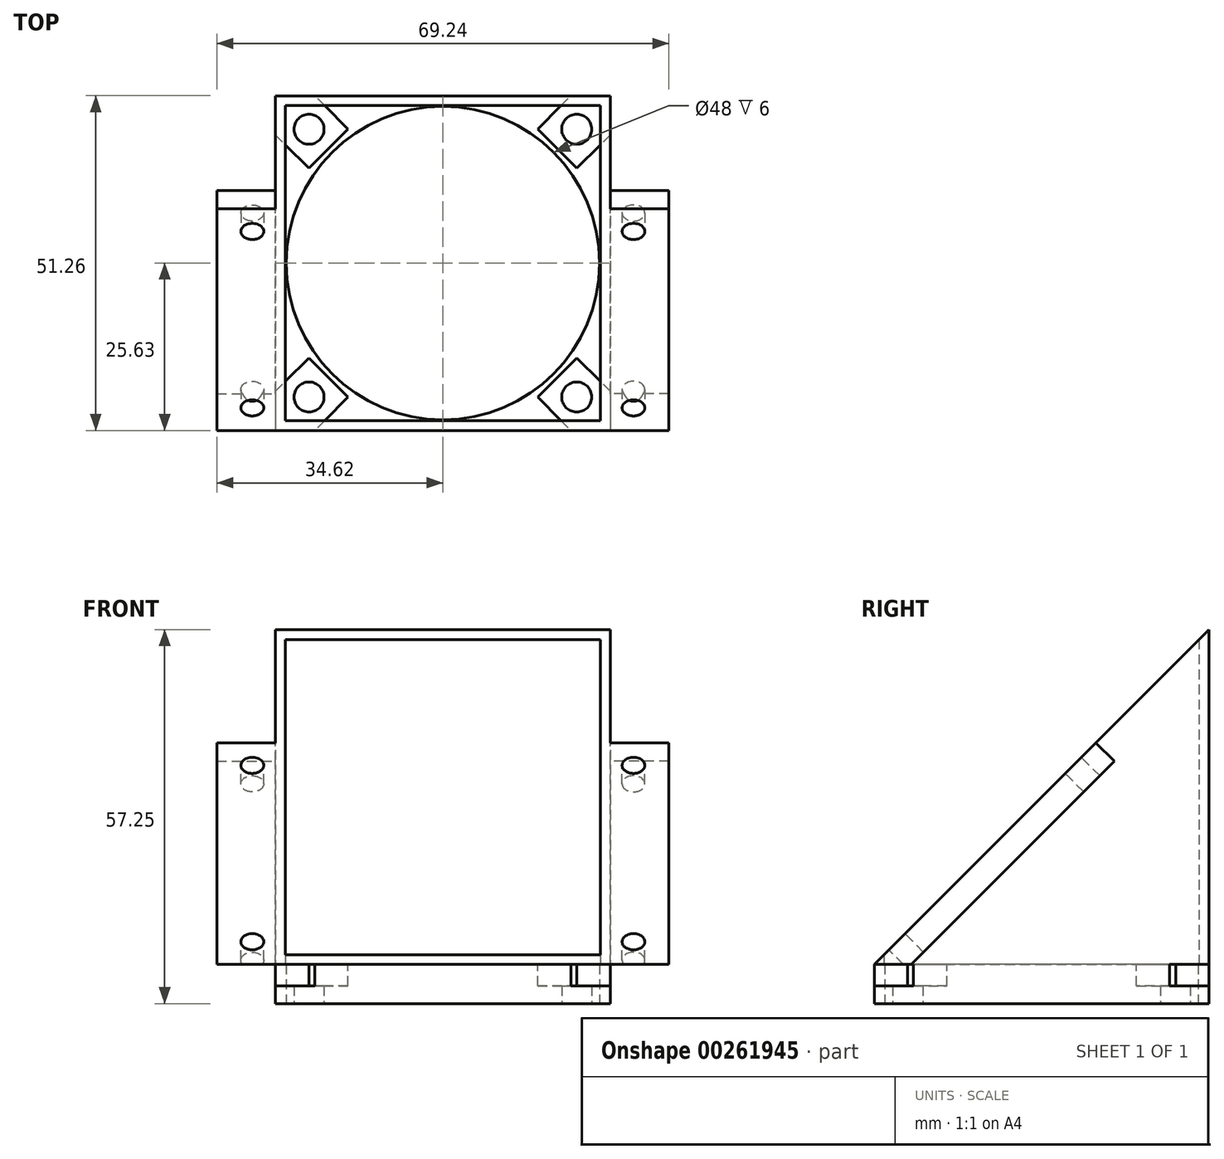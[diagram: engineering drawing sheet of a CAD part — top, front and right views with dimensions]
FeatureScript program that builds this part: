
annotation { "Feature Type Name" : "Feature", "Feature Type Description" : "" }
export const myFeature = defineFeature(function(context is Context, id is Id, definition is map)
    precondition{}
    {
        {
            var Q0;
            Q0=qCreatedBy(makeId("Top.planeOp"),FACE);
            var sketch = newSketch(context, id + "F0", { "sketchPlane" : qUnion([Q0])});
            skLineSegment(sketch, "E0.bottom", {"start": v(-25.63, 25.63) * mm, "end": v(25.63, 25.63) * mm});
            skLineSegment(sketch, "E0.top", {"start": v(-25.63, -25.63) * mm, "end": v(25.63, -25.63) * mm});
            skLineSegment(sketch, "E0.left", {"start": v(-25.63, 25.63) * mm, "end": v(-25.63, -25.63) * mm});
            skLineSegment(sketch, "E0.right", {"start": v(25.63, 25.63) * mm, "end": v(25.63, -25.63) * mm});
            skCircle(sketch, "E1", {"center": v(0, 0) * mm, "radius": 24 * mm});
            skLineSegment(sketch, "E2.bottom", {"start": v(-20.5, 20.5) * mm, "end": v(20.5, 20.5) * mm, "construction": true});
            skLineSegment(sketch, "E2.top", {"start": v(-20.5, -20.5) * mm, "end": v(20.5, -20.5) * mm, "construction": true});
            skLineSegment(sketch, "E2.left", {"start": v(-20.5, 20.5) * mm, "end": v(-20.5, -20.5) * mm, "construction": true});
            skLineSegment(sketch, "E2.right", {"start": v(20.5, 20.5) * mm, "end": v(20.5, -20.5) * mm, "construction": true});
            skCircle(sketch, "E3", {"center": v(-20.5, 20.5) * mm, "radius": 2.3 * mm});
            skCircle(sketch, "E4", {"center": v(20.5, 20.5) * mm, "radius": 2.3 * mm});
            skCircle(sketch, "E5", {"center": v(20.5, -20.5) * mm, "radius": 2.3 * mm});
            skCircle(sketch, "E6", {"center": v(-20.5, -20.5) * mm, "radius": 2.3 * mm});
            skSolve(sketch);
        }
        {
            var Q0;
            Q0 = qSketchRegion(id + "F0", true);
            extrude(context, id + "F1", {"entities" : qUnion([Q0]), "depth" : 6 * mm});
        }
        {
            var Q0;
            Q0=makeQuery(id+"F1.opExtrude","CAP_FACE",FACE,{"disambiguationData":[OSD([sQuery(id+"F0.wireOp",EDGE,"E0.bottom"),sQuery(id+"F0.wireOp",EDGE,"E0.top"),sQuery(id+"F0.wireOp",EDGE,"E0.left"),sQuery(id+"F0.wireOp",EDGE,"E0.right"),sQuery(id+"F0.wireOp",EDGE,"E1"),sQuery(id+"F0.wireOp",EDGE,"E3"),sQuery(id+"F0.wireOp",EDGE,"E4"),sQuery(id+"F0.wireOp",EDGE,"E5"),sQuery(id+"F0.wireOp",EDGE,"E6")])],"isStart":false});
            var sketch = newSketch(context, id + "F2", { "sketchPlane" : qUnion([Q0])});
            skLineSegment(sketch, "E7", {"start": v(25.62, 25.62) * mm, "end": v(-25.62, -25.62) * mm, "construction": true});
            skLineSegment(sketch, "E8", {"start": v(-25.62, 25.62) * mm, "end": v(25.62, -25.62) * mm, "construction": true});
            skLineSegment(sketch, "E9", {"start": v(-25.63, 19.61) * mm, "end": v(-20.54, 14.52) * mm});
            skLineSegment(sketch, "E10", {"start": v(-20.54, 14.52) * mm, "end": v(-14.52, 20.54) * mm});
            skLineSegment(sketch, "E11", {"start": v(-14.52, 20.54) * mm, "end": v(-19.61, 25.63) * mm});
            skLineSegment(sketch, "E12", {"start": v(-19.61, 25.63) * mm, "end": v(-25.62, 25.62) * mm});
            skLineSegment(sketch, "E13", {"start": v(-25.62, 25.62) * mm, "end": v(-25.63, 19.61) * mm});
            skPoint(sketch, "E14", {"position": v(-20.5, 20.5) * mm});
            skLineSegment(sketch, "E15.MirrorCS", {"start": v(14.52, 20.54) * mm, "end": v(19.61, 25.63) * mm});
            skLineSegment(sketch, "E16.MirrorCS", {"start": v(20.54, 14.52) * mm, "end": v(14.52, 20.54) * mm});
            skLineSegment(sketch, "E17.MirrorCS", {"start": v(25.63, 19.61) * mm, "end": v(20.54, 14.52) * mm});
            skLineSegment(sketch, "E18.MirrorCS", {"start": v(25.62, 25.62) * mm, "end": v(25.63, 19.61) * mm});
            skLineSegment(sketch, "E19.MirrorCS", {"start": v(19.61, 25.63) * mm, "end": v(25.62, 25.62) * mm});
            skLineSegment(sketch, "E20.MirrorCS", {"start": v(25.63, -19.61) * mm, "end": v(20.54, -14.52) * mm});
            skLineSegment(sketch, "E21.MirrorCS", {"start": v(20.54, -14.52) * mm, "end": v(14.52, -20.54) * mm});
            skLineSegment(sketch, "E22.MirrorCS", {"start": v(14.52, -20.54) * mm, "end": v(19.61, -25.63) * mm});
            skLineSegment(sketch, "E23.MirrorCS", {"start": v(19.61, -25.63) * mm, "end": v(25.62, -25.62) * mm});
            skLineSegment(sketch, "E24.MirrorCS", {"start": v(25.62, -25.62) * mm, "end": v(25.63, -19.61) * mm});
            skLineSegment(sketch, "E25.MirrorCS", {"start": v(-20.54, -14.52) * mm, "end": v(-14.52, -20.54) * mm});
            skLineSegment(sketch, "E26.MirrorCS", {"start": v(-14.52, -20.54) * mm, "end": v(-19.61, -25.63) * mm});
            skLineSegment(sketch, "E27.MirrorCS", {"start": v(-19.61, -25.63) * mm, "end": v(-25.62, -25.62) * mm});
            skLineSegment(sketch, "E28.MirrorCS", {"start": v(-25.62, -25.62) * mm, "end": v(-25.63, -19.61) * mm});
            skLineSegment(sketch, "E29.MirrorCS", {"start": v(-25.63, -19.61) * mm, "end": v(-20.54, -14.52) * mm});
            skSolve(sketch);
        }
        {
            var Q0;
            Q0 = qSketchRegion(id + "F2", true);
            extrude(context, id + "F3", {"entities" : qUnion([Q0]), "operationType" : NewBodyOperationType.REMOVE, "oppositeDirection" : true, "depth" : 3.3 * mm});
        }
        {
            var Q0;
            Q0=makeQuery(id+"F1.opExtrude","CAP_FACE",FACE,{"disambiguationData":[OSD([sQuery(id+"F0.wireOp",EDGE,"E0.bottom"),sQuery(id+"F0.wireOp",EDGE,"E0.top"),sQuery(id+"F0.wireOp",EDGE,"E0.left"),sQuery(id+"F0.wireOp",EDGE,"E0.right"),sQuery(id+"F0.wireOp",EDGE,"E1"),sQuery(id+"F0.wireOp",EDGE,"E3"),sQuery(id+"F0.wireOp",EDGE,"E4"),sQuery(id+"F0.wireOp",EDGE,"E5"),sQuery(id+"F0.wireOp",EDGE,"E6")])],"isStart":false});
            var sketch = newSketch(context, id + "F4", { "sketchPlane" : qUnion([Q0])});
            skLineSegment(sketch, "E30.bottom", {"start": v(-25.63, 25.63) * mm, "end": v(25.63, 25.63) * mm});
            skLineSegment(sketch, "E30.top", {"start": v(-25.63, -25.63) * mm, "end": v(25.63, -25.63) * mm});
            skLineSegment(sketch, "E30.left", {"start": v(-25.63, 25.63) * mm, "end": v(-25.63, -25.63) * mm});
            skLineSegment(sketch, "E30.right", {"start": v(25.63, 25.63) * mm, "end": v(25.63, -25.63) * mm});
            skLineSegment(sketch, "E31.0", {"start": v(-24.12, 24.12) * mm, "end": v(24.12, 24.12) * mm});
            skLineSegment(sketch, "E31.1", {"start": v(-24.12, 24.12) * mm, "end": v(-24.12, -24.12) * mm});
            skLineSegment(sketch, "E31.2", {"start": v(-24.12, -24.12) * mm, "end": v(24.12, -24.12) * mm});
            skLineSegment(sketch, "E31.3", {"start": v(24.12, 24.12) * mm, "end": v(24.12, -24.12) * mm});
            skSolve(sketch);
        }
        {
            var Q0;
            Q0 = qSketchRegion(id + "F4", true);
            extrude(context, id + "F5", {"entities" : qUnion([Q0]), "operationType" : NewBodyOperationType.ADD, "depth" : 55 * mm});
        }
        {
            var Q0;
            Q0=makeQuery(id+"F5.boolean.opBoolean","MERGE",FACE,{"derivedFrom":[makeQuery(id+"F1.opExtrude","SWEPT_FACE",FACE,{"disambiguationData":[OSD([sQuery(id+"F0.wireOp",EDGE,"E0.right")])]}),makeQuery(id+"F5.opExtrude","SWEPT_FACE",FACE,{"disambiguationData":[OSD([sQuery(id+"F4.wireOp",EDGE,"E30.right")])]})]});
            var sketch = newSketch(context, id + "F6", { "sketchPlane" : qUnion([Q0])});
            skLineSegment(sketch, "E32", {"start": v(-25.63, 6) * mm, "end": v(25.63, 57.25) * mm});
            skLineSegment(sketch, "E33", {"start": v(25.63, 57.25) * mm, "end": v(25.63, 61) * mm});
            skLineSegment(sketch, "E34", {"start": v(25.63, 61) * mm, "end": v(-25.63, 61) * mm});
            skLineSegment(sketch, "E35", {"start": v(-25.63, 61) * mm, "end": v(-25.63, 6) * mm});
            skSolve(sketch);
        }
        {
            var Q0;
            Q0 = qSketchRegion(id + "F6", true);
            extrude(context, id + "F7", {"entities" : qUnion([Q0]), "operationType" : NewBodyOperationType.REMOVE, "endBound" : BoundingType.THROUGH_ALL, "oppositeDirection" : true, "depth" : 25 * mm});
        }
        {
            var Q0;
            Q0=makeQuery(id+"F5.boolean.opBoolean","MERGE",FACE,{"derivedFrom":[makeQuery(id+"F1.opExtrude","SWEPT_FACE",FACE,{"disambiguationData":[OSD([sQuery(id+"F0.wireOp",EDGE,"E0.right")])]}),makeQuery(id+"F5.opExtrude","SWEPT_FACE",FACE,{"disambiguationData":[OSD([sQuery(id+"F4.wireOp",EDGE,"E30.right")])]})]});
            var sketch = newSketch(context, id + "F8", { "sketchPlane" : qUnion([Q0])});
            skLineSegment(sketch, "E36", {"start": v(-25.63, 6) * mm, "end": v(-19.97, 6) * mm});
            skPoint(sketch, "E36.endSnap0", {"position": v(-22.62, 6) * mm});
            skLineSegment(sketch, "E37", {"start": v(-19.97, 6) * mm, "end": v(11.14, 37.11) * mm});
            skLineSegment(sketch, "E38", {"start": v(11.14, 37.11) * mm, "end": v(8.32, 39.94) * mm});
            skLineSegment(sketch, "E39", {"start": v(8.32, 39.94) * mm, "end": v(-25.63, 6) * mm});
            skSolve(sketch);
        }
        {
            var Q0;
            Q0 = qSketchRegion(id + "F8", true);
            extrude(context, id + "F9", {"entities" : qUnion([Q0]), "operationType" : NewBodyOperationType.ADD, "depth" : 9 * mm});
        }
        {
            var Q0;
            Q0=makeQuery(id+"F5.boolean.opBoolean","MERGE",FACE,{"derivedFrom":[makeQuery(id+"F1.opExtrude","SWEPT_FACE",FACE,{"disambiguationData":[OSD([sQuery(id+"F0.wireOp",EDGE,"E0.left")])]}),makeQuery(id+"F5.opExtrude","SWEPT_FACE",FACE,{"disambiguationData":[OSD([sQuery(id+"F4.wireOp",EDGE,"E30.left")])]})]});
            var sketch = newSketch(context, id + "F10", { "sketchPlane" : qUnion([Q0])});
            skLineSegment(sketch, "E40", {"start": v(25.62, 6) * mm, "end": v(19.97, 6) * mm});
            skLineSegment(sketch, "E41", {"start": v(19.97, 6) * mm, "end": v(-11.14, 37.11) * mm});
            skLineSegment(sketch, "E42", {"start": v(-11.14, 37.11) * mm, "end": v(-8.32, 39.94) * mm});
            skLineSegment(sketch, "E43", {"start": v(-8.32, 39.94) * mm, "end": v(25.62, 6) * mm});
            skSolve(sketch);
        }
        {
            var Q0;
            Q0 = qSketchRegion(id + "F10", true);
            extrude(context, id + "F11", {"entities" : qUnion([Q0]), "operationType" : NewBodyOperationType.ADD, "depth" : 9 * mm});
        }
        {
            var Q0;
            Q0=makeQuery(id+"F11.boolean.opBoolean","MERGE",FACE,{"derivedFrom":[makeQuery(id+"F9.boolean.opBoolean","MERGE",FACE,{"derivedFrom":[makeQuery(id+"F7.boolean.opBoolean","COPY",FACE,{"derivedFrom":makeQuery(id+"F7.opExtrude","SWEPT_FACE",FACE,{"disambiguationData":[OSD([sQuery(id+"F6.wireOp",EDGE,"E32")])]})}),makeQuery(id+"F9.opExtrude","SWEPT_FACE",FACE,{"disambiguationData":[OSD([sQuery(id+"F8.wireOp",EDGE,"E39")])]})]}),makeQuery(id+"F11.opExtrude","SWEPT_FACE",FACE,{"disambiguationData":[OSD([sQuery(id+"F10.wireOp",EDGE,"E43")])]})]});
            var sketch = newSketch(context, id + "F12", { "sketchPlane" : qUnion([Q0])});
            skLineSegment(sketch, "E44.bottom", {"start": v(29.2, 29.22) * mm, "end": v(-29.2, 29.22) * mm, "construction": true});
            skLineSegment(sketch, "E44.top", {"start": v(29.2, -8.98) * mm, "end": v(-29.2, -8.98) * mm, "construction": true});
            skLineSegment(sketch, "E44.left", {"start": v(29.2, 29.22) * mm, "end": v(29.2, -8.98) * mm, "construction": true});
            skLineSegment(sketch, "E44.right", {"start": v(-29.2, 29.22) * mm, "end": v(-29.2, -8.98) * mm, "construction": true});
            skLineSegment(sketch, "E45", {"start": v(0, -13.88) * mm, "end": v(0, 73.2) * mm, "construction": true});
            skPoint(sketch, "E45.endSnap0", {"position": v(0, -11.76) * mm});
            skLineSegment(sketch, "E46", {"start": v(38.9, 10.12) * mm, "end": v(-43.67, 10.12) * mm, "construction": true});
            skPoint(sketch, "E46.startSnap0", {"position": v(34.62, 10.12) * mm});
            skCircle(sketch, "E47", {"center": v(29.2, 29.22) * mm, "radius": 1.75 * mm});
            skCircle(sketch, "E48", {"center": v(29.2, -8.98) * mm, "radius": 1.75 * mm});
            skCircle(sketch, "E49", {"center": v(-29.2, 29.22) * mm, "radius": 1.75 * mm});
            skCircle(sketch, "E50", {"center": v(-29.2, -8.98) * mm, "radius": 1.75 * mm});
            skSolve(sketch);
        }
        {
            var Q0;
            Q0 = qSketchRegion(id + "F12", true);
            extrude(context, id + "F13", {"entities" : qUnion([Q0]), "operationType" : NewBodyOperationType.REMOVE, "endBound" : BoundingType.THROUGH_ALL, "oppositeDirection" : true, "depth" : 25 * mm});
        }
    });
